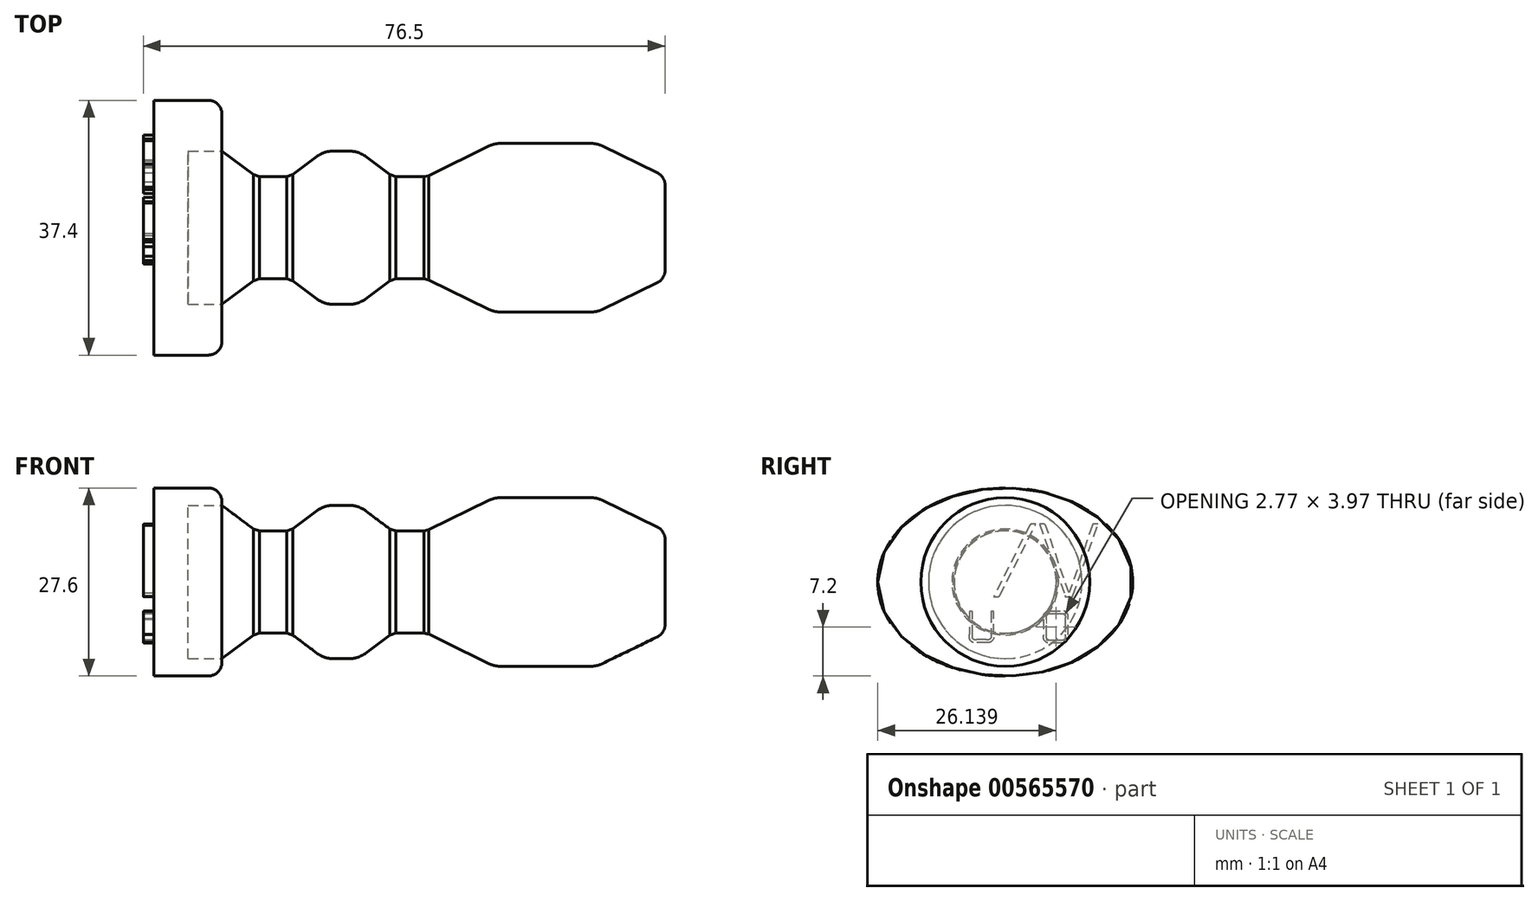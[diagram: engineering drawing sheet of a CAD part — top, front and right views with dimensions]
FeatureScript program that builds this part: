
annotation { "Feature Type Name" : "Feature", "Feature Type Description" : "" }
export const myFeature = defineFeature(function(context is Context, id is Id, definition is map)
    precondition{}
    {
        {
            var Q0;
            Q0=qCreatedBy(makeId("Top.planeOp"),FACE);
            var sketch = newSketch(context, id + "F0", { "sketchPlane" : qUnion([Q0])});
            skLineSegment(sketch, "E0", {"start": v(0, 0) * mm, "end": v(0, -25) * mm});
            skLineSegment(sketch, "E1", {"start": v(0, -25) * mm, "end": v(10, -25) * mm});
            skLineSegment(sketch, "E2", {"start": v(10, -25) * mm, "end": v(10, -11.25) * mm});
            skLineSegment(sketch, "E3", {"start": v(10, -11.25) * mm, "end": v(15, -7.5) * mm});
            skLineSegment(sketch, "E4", {"start": v(15, -7.5) * mm, "end": v(20, -7.5) * mm});
            skLineSegment(sketch, "E5", {"start": v(20, -7.5) * mm, "end": v(25, -11.25) * mm});
            skLineSegment(sketch, "E6", {"start": v(25, -11.25) * mm, "end": v(30, -11.25) * mm});
            skLineSegment(sketch, "E7", {"start": v(30, -11.25) * mm, "end": v(35, -7.5) * mm});
            skLineSegment(sketch, "E8", {"start": v(35, -7.5) * mm, "end": v(40, -7.5) * mm});
            skLineSegment(sketch, "E9", {"start": v(40, -7.5) * mm, "end": v(50, -12.38) * mm});
            skLineSegment(sketch, "E10", {"start": v(50, -12.38) * mm, "end": v(65, -12.38) * mm});
            skLineSegment(sketch, "E11", {"start": v(65, -12.38) * mm, "end": v(75, -7.5) * mm});
            skLineSegment(sketch, "E12", {"start": v(75, -7.5) * mm, "end": v(75, 0) * mm});
            skLineSegment(sketch, "E13", {"start": v(75, 0) * mm, "end": v(0, 0) * mm});
            skLineSegment(sketch, "E14", {"start": v(10, -11.25) * mm, "end": v(10, 0) * mm});
            skLineSegment(sketch, "E15", {"start": v(10, -11.25) * mm, "end": v(0, -11.25) * mm});
            skLineSegment(sketch, "E16", {"start": v(5.06, 0) * mm, "end": v(5.06, -11.25) * mm});
            skLineSegment(sketch, "E17", {"start": v(0, -11.45) * mm, "end": v(10, -11.45) * mm});
            skLineSegment(sketch, "E18", {"start": v(5.06, -11.25) * mm, "end": v(5.06, -11.45) * mm});
            skSolve(sketch);
        }
        {
            var Q0;
            Q0=makeQuery(id+"F0.imprint","IMPRINT",FACE,{"disambiguationData":[TD([[makeQuery(id+"F0.imprint","IMPRINT",EDGE,{"derivedFrom":sQuery(id+"F0.wireOp",EDGE,"E3")}),1.0]])]});
            var Q1;
            {var subQ0=sQuery(id+"F0.wireOp",EDGE,"E14");Q1=makeQuery(id+"F0.imprint","IMPRINT",FACE,{"disambiguationData":[TD([[makeQuery(id+"F0.imprint","IMPRINT",EDGE,{"derivedFrom":subQ0}),1.0]])]});}
            var Q2;
            Q2=sQuery(id+"F0.wireOp",EDGE,"E13");
            revolve(context, id + "F1", {"entities" : qUnion([Q0, Q1]), "axis" : qUnion([Q2]), "revolveType" : RevolveType.FULL});
        }
        {
            var Q0;
            Q0=qCreatedBy(makeId("Right.planeOp"),FACE);
            var sketch = newSketch(context, id + "F2", { "sketchPlane" : qUnion([Q0])});
            skEllipse(sketch, "E19", {"center": v(0, 0) * mm, "majorRadius": 18.7 * mm, "minorRadius": 13.8 * mm, "majorAxis": v(-1, 0)});
            skSolve(sketch);
        }
        {
            var Q0;
            Q0=makeQuery(id+"F2.imprint","IMPRINT",FACE,{"disambiguationData":[TD([[makeQuery(id+"F2.imprint","IMPRINT",EDGE,{"derivedFrom":sQuery(id+"F2.wireOp",EDGE,"E19")}),1.0]])]});
            extrude(context, id + "F3", {"entities" : qUnion([Q0]), "depth" : 10 * mm, "offsetDistance" : 25 * mm});
        }
        {
            var Q0;
            Q0=qCreatedBy(makeId("Right.planeOp"),FACE);
            var sketch = newSketch(context, id + "F4", { "sketchPlane" : qUnion([Q0])});
            skLineSegment(sketch, "E20", {"start": v(-0.44, 1.05) * mm, "end": v(-0.95, 0.16) * mm});
            skLineSegment(sketch, "E21", {"start": v(-0.95, 0.16) * mm, "end": v(-1.46, 1.05) * mm});
            skFitSpline(sketch, "E22", {"points": [v(-1.46, 1.05) * mm, v(-1.46, 1.06) * mm, v(-1.47, 1.06) * mm, v(-1.48, 1.06) * mm]});
            skLineSegment(sketch, "E23", {"start": v(-1.48, 1.06) * mm, "end": v(-1.59, 1.06) * mm});
            skLineSegment(sketch, "E24", {"start": v(-1.59, 1.06) * mm, "end": v(-1.59, -0.27) * mm});
            skLineSegment(sketch, "E25", {"start": v(-1.59, -0.27) * mm, "end": v(-1.52, -0.27) * mm});
            skFitSpline(sketch, "E26", {"points": [v(-1.52, -0.27) * mm, v(-1.5, -0.27) * mm, v(-1.5, -0.26) * mm, v(-1.5, -0.25) * mm]});
            skLineSegment(sketch, "E27", {"start": v(-1.5, -0.25) * mm, "end": v(-1.5, 0.94) * mm});
            skLineSegment(sketch, "E28", {"start": v(-1.5, 0.94) * mm, "end": v(-1.02, 0.1) * mm});
            skFitSpline(sketch, "E29", {"points": [v(-1.02, 0.1) * mm, v(-1.02, 0.08) * mm, v(-1, 0.08) * mm, v(-1, 0.08) * mm]});
            skLineSegment(sketch, "E30", {"start": v(-1, 0.08) * mm, "end": v(-0.91, 0.08) * mm});
            skFitSpline(sketch, "E31", {"points": [v(-0.91, 0.08) * mm, v(-0.9, 0.08) * mm, v(-0.9, 0.08) * mm, v(-0.89, 0.1) * mm]});
            skLineSegment(sketch, "E32", {"start": v(-0.4, 0.94) * mm, "end": v(-0.4, -0.25) * mm});
            skFitSpline(sketch, "E33", {"points": [v(-0.4, -0.25) * mm, v(-0.4, -0.26) * mm, v(-0.4, -0.27) * mm, v(-0.39, -0.27) * mm]});
            skLineSegment(sketch, "E34", {"start": v(-0.39, -0.27) * mm, "end": v(-0.32, -0.27) * mm});
            skLineSegment(sketch, "E35", {"start": v(-0.32, -0.27) * mm, "end": v(-0.32, 1.06) * mm});
            skLineSegment(sketch, "E36", {"start": v(-0.32, 1.06) * mm, "end": v(-0.43, 1.06) * mm});
            skFitSpline(sketch, "E37", {"points": [v(-0.43, 1.06) * mm, v(-0.43, 1.06) * mm, v(-0.44, 1.06) * mm, v(-0.44, 1.05) * mm]});
            skLineSegment(sketch, "E38", {"start": v(0.45, 1.04) * mm, "end": v(-0.21, -0.27) * mm});
            skLineSegment(sketch, "E39", {"start": v(-0.21, -0.27) * mm, "end": v(-0.14, -0.27) * mm});
            skFitSpline(sketch, "E40", {"points": [v(-0.14, -0.27) * mm, v(-0.13, -0.27) * mm, v(-0.11, -0.26) * mm, v(-0.1, -0.25) * mm]});
            skLineSegment(sketch, "E41", {"start": v(-0.1, -0.25) * mm, "end": v(0.56, 1.06) * mm});
            skLineSegment(sketch, "E42", {"start": v(0.56, 1.06) * mm, "end": v(0.48, 1.06) * mm});
            skFitSpline(sketch, "E43", {"points": [v(0.48, 1.06) * mm, v(0.47, 1.06) * mm, v(0.46, 1.05) * mm, v(0.45, 1.04) * mm]});
            skFitSpline(sketch, "E44", {"points": [v(1.1, -0.25) * mm, v(1.1, -0.26) * mm, v(1.1, -0.27) * mm, v(1.12, -0.27) * mm]});
            skLineSegment(sketch, "E45", {"start": v(1.12, -0.27) * mm, "end": v(1.22, -0.27) * mm});
            skFitSpline(sketch, "E46", {"points": [v(1.22, -0.27) * mm, v(1.23, -0.27) * mm, v(1.24, -0.26) * mm, v(1.24, -0.25) * mm]});
            skLineSegment(sketch, "E47", {"start": v(1.24, -0.25) * mm, "end": v(1.7, 1.06) * mm});
            skLineSegment(sketch, "E48", {"start": v(1.7, 1.06) * mm, "end": v(1.63, 1.06) * mm});
            skFitSpline(sketch, "E49", {"points": [v(1.63, 1.06) * mm, v(1.62, 1.06) * mm, v(1.6, 1.05) * mm, v(1.6, 1.04) * mm]});
            skLineSegment(sketch, "E50", {"start": v(1.6, 1.04) * mm, "end": v(1.17, -0.2) * mm});
            skLineSegment(sketch, "E51", {"start": v(1.17, -0.2) * mm, "end": v(0.74, 1.04) * mm});
            skFitSpline(sketch, "E52", {"points": [v(0.74, 1.04) * mm, v(0.73, 1.05) * mm, v(0.72, 1.06) * mm, v(0.7, 1.06) * mm]});
            skLineSegment(sketch, "E53", {"start": v(0.7, 1.06) * mm, "end": v(0.63, 1.06) * mm});
            skLineSegment(sketch, "E54", {"start": v(0.63, 1.06) * mm, "end": v(1.1, -0.25) * mm});
            skLineSegment(sketch, "E55", {"start": v(-1.2, -0.9) * mm, "end": v(-1.2, -0.98) * mm});
            skFitSpline(sketch, "E56", {"points": [v(-1.2, -0.98) * mm, v(-1.2, -1.03) * mm, v(-1.25, -1.06) * mm, v(-1.3, -1.06) * mm]});
            skLineSegment(sketch, "E57", {"start": v(-1.3, -1.06) * mm, "end": v(-1.58, -1.06) * mm});
            skFitSpline(sketch, "E58", {"points": [v(-1.58, -1.06) * mm, v(-1.59, -1.06) * mm, v(-1.6, -1.06) * mm, v(-1.6, -1.07) * mm]});
            skLineSegment(sketch, "E59", {"start": v(-1.6, -1.07) * mm, "end": v(-1.6, -1.1) * mm});
            skLineSegment(sketch, "E60", {"start": v(-1.6, -1.1) * mm, "end": v(-1.3, -1.1) * mm});
            skFitSpline(sketch, "E61", {"points": [v(-1.3, -1.1) * mm, v(-1.22, -1.1) * mm, v(-1.15, -1.06) * mm, v(-1.15, -0.98) * mm]});
            skLineSegment(sketch, "E62", {"start": v(-1.15, -0.98) * mm, "end": v(-1.15, -0.9) * mm});
            skFitSpline(sketch, "E63", {"points": [v(-1.15, -0.9) * mm, v(-1.15, -0.88) * mm, v(-1.17, -0.86) * mm, v(-1.18, -0.85) * mm]});
            skLineSegment(sketch, "E64", {"start": v(-1.18, -0.85) * mm, "end": v(-1.53, -0.73) * mm});
            skFitSpline(sketch, "E65", {"points": [v(-1.53, -0.73) * mm, v(-1.54, -0.73) * mm, v(-1.54, -0.72) * mm, v(-1.54, -0.71) * mm]});
            skLineSegment(sketch, "E66", {"start": v(-1.54, -0.71) * mm, "end": v(-1.54, -0.67) * mm});
            skFitSpline(sketch, "E67", {"points": [v(-1.54, -0.67) * mm, v(-1.54, -0.62) * mm, v(-1.5, -0.6) * mm, v(-1.45, -0.6) * mm]});
            skLineSegment(sketch, "E68", {"start": v(-1.45, -0.6) * mm, "end": v(-1.2, -0.6) * mm});
            skFitSpline(sketch, "E69", {"points": [v(-1.2, -0.6) * mm, v(-1.2, -0.6) * mm, v(-1.2, -0.58) * mm, v(-1.2, -0.58) * mm]});
            skLineSegment(sketch, "E70", {"start": v(-1.2, -0.58) * mm, "end": v(-1.2, -0.54) * mm});
            skLineSegment(sketch, "E71", {"start": v(-1.2, -0.54) * mm, "end": v(-1.45, -0.54) * mm});
            skFitSpline(sketch, "E72", {"points": [v(-1.45, -0.54) * mm, v(-1.53, -0.54) * mm, v(-1.6, -0.6) * mm, v(-1.6, -0.67) * mm]});
            skLineSegment(sketch, "E73", {"start": v(-1.6, -0.67) * mm, "end": v(-1.6, -0.73) * mm});
            skFitSpline(sketch, "E74", {"points": [v(-1.6, -0.73) * mm, v(-1.6, -0.74) * mm, v(-1.58, -0.76) * mm, v(-1.56, -0.77) * mm]});
            skLineSegment(sketch, "E75", {"start": v(-1.56, -0.77) * mm, "end": v(-1.21, -0.9) * mm});
            skFitSpline(sketch, "E76", {"points": [v(-1.21, -0.9) * mm, v(-1.2, -0.9) * mm, v(-1.2, -0.9) * mm, v(-1.2, -0.9) * mm]});
            skLineSegment(sketch, "E77", {"start": v(-0.78, -1.06) * mm, "end": v(-0.88, -1.06) * mm});
            skFitSpline(sketch, "E78", {"points": [v(-0.88, -1.06) * mm, v(-0.93, -1.06) * mm, v(-0.97, -1.02) * mm, v(-0.97, -0.97) * mm]});
            skLineSegment(sketch, "E79", {"start": v(-0.97, -0.97) * mm, "end": v(-0.97, -0.6) * mm});
            skLineSegment(sketch, "E80", {"start": v(-0.97, -0.6) * mm, "end": v(-0.81, -0.6) * mm});
            skFitSpline(sketch, "E81", {"points": [v(-0.81, -0.6) * mm, v(-0.8, -0.6) * mm, v(-0.8, -0.59) * mm, v(-0.8, -0.58) * mm]});
            skLineSegment(sketch, "E82", {"start": v(-0.8, -0.58) * mm, "end": v(-0.8, -0.55) * mm});
            skLineSegment(sketch, "E83", {"start": v(-0.8, -0.55) * mm, "end": v(-0.94, -0.55) * mm});
            skFitSpline(sketch, "E84", {"points": [v(-0.94, -0.55) * mm, v(-0.95, -0.55) * mm, v(-0.97, -0.55) * mm, v(-0.97, -0.57) * mm]});
            skLineSegment(sketch, "E85", {"start": v(-0.97, -0.57) * mm, "end": v(-0.97, -0.27) * mm});
            skFitSpline(sketch, "E86", {"points": [v(-0.97, -0.27) * mm, v(-0.97, -0.27) * mm, v(-0.97, -0.26) * mm, v(-0.98, -0.26) * mm]});
            skLineSegment(sketch, "E87", {"start": v(-0.98, -0.26) * mm, "end": v(-1.02, -0.26) * mm});
            skLineSegment(sketch, "E88", {"start": v(-1.02, -0.26) * mm, "end": v(-1.02, -0.96) * mm});
            skFitSpline(sketch, "E89", {"points": [v(-1.02, -0.96) * mm, v(-1.02, -1.04) * mm, v(-0.96, -1.1) * mm, v(-0.88, -1.1) * mm]});
            skLineSegment(sketch, "E90", {"start": v(-0.88, -1.1) * mm, "end": v(-0.77, -1.1) * mm});
            skLineSegment(sketch, "E91", {"start": v(-0.77, -1.1) * mm, "end": v(-0.77, -1.07) * mm});
            skFitSpline(sketch, "E92", {"points": [v(-0.77, -1.07) * mm, v(-0.77, -1.06) * mm, v(-0.77, -1.06) * mm, v(-0.78, -1.06) * mm]});
            skFitSpline(sketch, "E93", {"points": [v(-0.66, -0.96) * mm, v(-0.66, -1.04) * mm, v(-0.6, -1.1) * mm, v(-0.52, -1.1) * mm]});
            skLineSegment(sketch, "E94", {"start": v(-0.52, -1.1) * mm, "end": v(-0.35, -1.1) * mm});
            skFitSpline(sketch, "E95", {"points": [v(-0.35, -1.1) * mm, v(-0.28, -1.1) * mm, v(-0.21, -1.04) * mm, v(-0.21, -0.96) * mm]});
            skLineSegment(sketch, "E96", {"start": v(-0.21, -0.96) * mm, "end": v(-0.21, -0.54) * mm});
            skLineSegment(sketch, "E97", {"start": v(-0.21, -0.54) * mm, "end": v(-0.25, -0.54) * mm});
            skFitSpline(sketch, "E98", {"points": [v(-0.25, -0.54) * mm, v(-0.26, -0.54) * mm, v(-0.26, -0.55) * mm, v(-0.26, -0.56) * mm]});
            skLineSegment(sketch, "E99", {"start": v(-0.26, -0.56) * mm, "end": v(-0.26, -0.97) * mm});
            skFitSpline(sketch, "E100", {"points": [v(-0.26, -0.97) * mm, v(-0.26, -1.02) * mm, v(-0.3, -1.06) * mm, v(-0.35, -1.06) * mm]});
            skLineSegment(sketch, "E101", {"start": v(-0.35, -1.06) * mm, "end": v(-0.52, -1.06) * mm});
            skFitSpline(sketch, "E102", {"points": [v(-0.52, -1.06) * mm, v(-0.57, -1.06) * mm, v(-0.6, -1.02) * mm, v(-0.6, -0.97) * mm]});
            skLineSegment(sketch, "E103", {"start": v(-0.6, -0.97) * mm, "end": v(-0.6, -0.56) * mm});
            skFitSpline(sketch, "E104", {"points": [v(-0.6, -0.56) * mm, v(-0.6, -0.55) * mm, v(-0.61, -0.54) * mm, v(-0.62, -0.54) * mm]});
            skLineSegment(sketch, "E105", {"start": v(-0.62, -0.54) * mm, "end": v(-0.66, -0.54) * mm});
            skLineSegment(sketch, "E106", {"start": v(-0.66, -0.54) * mm, "end": v(-0.66, -0.96) * mm});
            skFitSpline(sketch, "E107", {"points": [v(0.32, -0.26) * mm, v(0.31, -0.26) * mm, v(0.3, -0.27) * mm, v(0.3, -0.28) * mm]});
            skLineSegment(sketch, "E108", {"start": v(0.3, -0.28) * mm, "end": v(0.3, -0.57) * mm});
            skFitSpline(sketch, "E109", {"points": [v(0.3, -0.57) * mm, v(0.3, -0.55) * mm, v(0.3, -0.54) * mm, v(0.28, -0.54) * mm]});
            skLineSegment(sketch, "E110", {"start": v(0.28, -0.54) * mm, "end": v(0.06, -0.54) * mm});
            skFitSpline(sketch, "E111", {"points": [v(0.06, -0.54) * mm, v(-0.02, -0.54) * mm, v(-0.08, -0.6) * mm, v(-0.08, -0.68) * mm]});
            skLineSegment(sketch, "E112", {"start": v(-0.08, -0.68) * mm, "end": v(-0.08, -0.96) * mm});
            skFitSpline(sketch, "E113", {"points": [v(-0.08, -0.96) * mm, v(-0.08, -1.04) * mm, v(-0.02, -1.1) * mm, v(0.06, -1.1) * mm]});
            skLineSegment(sketch, "E114", {"start": v(0.06, -1.1) * mm, "end": v(0.35, -1.1) * mm});
            skFitSpline(sketch, "E115", {"points": [v(0.35, -1.1) * mm, v(0.35, -1.1) * mm, v(0.36, -1.1) * mm, v(0.36, -1.1) * mm]});
            skLineSegment(sketch, "E116", {"start": v(0.36, -1.1) * mm, "end": v(0.36, -0.26) * mm});
            skLineSegment(sketch, "E117", {"start": v(0.36, -0.26) * mm, "end": v(0.32, -0.26) * mm});
            skFitSpline(sketch, "E118", {"points": [v(0.06, -1.06) * mm, v(0, -1.06) * mm, v(-0.03, -1.02) * mm, v(-0.03, -0.97) * mm]});
            skLineSegment(sketch, "E119", {"start": v(-0.03, -0.97) * mm, "end": v(-0.03, -0.68) * mm});
            skFitSpline(sketch, "E120", {"points": [v(-0.03, -0.68) * mm, v(-0.03, -0.63) * mm, v(0, -0.6) * mm, v(0.06, -0.6) * mm]});
            skLineSegment(sketch, "E121", {"start": v(0.06, -0.6) * mm, "end": v(0.29, -0.6) * mm});
            skFitSpline(sketch, "E122", {"points": [v(0.29, -0.6) * mm, v(0.3, -0.6) * mm, v(0.3, -0.6) * mm, v(0.3, -0.61) * mm]});
            skLineSegment(sketch, "E123", {"start": v(0.3, -0.61) * mm, "end": v(0.3, -1.06) * mm});
            skLineSegment(sketch, "E124", {"start": v(0.3, -1.06) * mm, "end": v(0.06, -1.06) * mm});
            skFitSpline(sketch, "E125", {"points": [v(0.5, -1.1) * mm, v(0.5, -1.1) * mm, v(0.5, -1.1) * mm, v(0.5, -1.1) * mm]});
            skLineSegment(sketch, "E126", {"start": v(0.5, -1.1) * mm, "end": v(0.55, -1.1) * mm});
            skLineSegment(sketch, "E127", {"start": v(0.55, -1.1) * mm, "end": v(0.55, -0.56) * mm});
            skFitSpline(sketch, "E128", {"points": [v(0.55, -0.56) * mm, v(0.55, -0.55) * mm, v(0.54, -0.54) * mm, v(0.53, -0.54) * mm]});
            skLineSegment(sketch, "E129", {"start": v(0.53, -0.54) * mm, "end": v(0.5, -0.54) * mm});
            skLineSegment(sketch, "E130", {"start": v(0.5, -0.54) * mm, "end": v(0.5, -1.1) * mm});
            skFitSpline(sketch, "E131", {"points": [v(0.5, -0.35) * mm, v(0.5, -0.36) * mm, v(0.5, -0.36) * mm, v(0.5, -0.36) * mm]});
            skLineSegment(sketch, "E132", {"start": v(0.5, -0.36) * mm, "end": v(0.55, -0.36) * mm});
            skLineSegment(sketch, "E133", {"start": v(0.55, -0.36) * mm, "end": v(0.55, -0.3) * mm});
            skFitSpline(sketch, "E134", {"points": [v(0.55, -0.3) * mm, v(0.55, -0.3) * mm, v(0.54, -0.3) * mm, v(0.54, -0.3) * mm]});
            skLineSegment(sketch, "E135", {"start": v(0.54, -0.3) * mm, "end": v(0.5, -0.3) * mm});
            skLineSegment(sketch, "E136", {"start": v(0.5, -0.3) * mm, "end": v(0.5, -0.35) * mm});
            skFitSpline(sketch, "E137", {"points": [v(1.01, -1.11) * mm, v(1.1, -1.11) * mm, v(1.15, -1.05) * mm, v(1.15, -0.97) * mm]});
            skLineSegment(sketch, "E138", {"start": v(1.15, -0.97) * mm, "end": v(1.15, -0.68) * mm});
            skFitSpline(sketch, "E139", {"points": [v(1.15, -0.68) * mm, v(1.15, -0.6) * mm, v(1.1, -0.54) * mm, v(1.01, -0.54) * mm]});
            skLineSegment(sketch, "E140", {"start": v(1.01, -0.54) * mm, "end": v(0.84, -0.54) * mm});
            skFitSpline(sketch, "E141", {"points": [v(0.84, -0.54) * mm, v(0.77, -0.54) * mm, v(0.7, -0.6) * mm, v(0.7, -0.68) * mm]});
            skLineSegment(sketch, "E142", {"start": v(0.7, -0.68) * mm, "end": v(0.7, -0.97) * mm});
            skFitSpline(sketch, "E143", {"points": [v(0.7, -0.97) * mm, v(0.7, -1.05) * mm, v(0.77, -1.11) * mm, v(0.84, -1.11) * mm]});
            skLineSegment(sketch, "E144", {"start": v(0.84, -1.11) * mm, "end": v(1.01, -1.11) * mm});
            skFitSpline(sketch, "E145", {"points": [v(1.01, -0.58) * mm, v(1.06, -0.58) * mm, v(1.1, -0.62) * mm, v(1.1, -0.67) * mm]});
            skLineSegment(sketch, "E146", {"start": v(1.1, -0.67) * mm, "end": v(1.1, -0.98) * mm});
            skFitSpline(sketch, "E147", {"points": [v(1.1, -0.98) * mm, v(1.1, -1.03) * mm, v(1.06, -1.07) * mm, v(1.01, -1.07) * mm]});
            skLineSegment(sketch, "E148", {"start": v(1.01, -1.07) * mm, "end": v(0.84, -1.07) * mm});
            skFitSpline(sketch, "E149", {"points": [v(0.84, -1.07) * mm, v(0.8, -1.07) * mm, v(0.76, -1.03) * mm, v(0.76, -0.98) * mm]});
            skLineSegment(sketch, "E150", {"start": v(0.76, -0.98) * mm, "end": v(0.76, -0.67) * mm});
            skFitSpline(sketch, "E151", {"points": [v(0.76, -0.67) * mm, v(0.76, -0.62) * mm, v(0.8, -0.58) * mm, v(0.84, -0.58) * mm]});
            skLineSegment(sketch, "E152", {"start": v(0.84, -0.58) * mm, "end": v(1.01, -0.58) * mm});
            skLineSegment(sketch, "E153", {"start": v(1.67, -0.9) * mm, "end": v(1.67, -0.98) * mm});
            skFitSpline(sketch, "E154", {"points": [v(1.67, -0.98) * mm, v(1.67, -1.03) * mm, v(1.63, -1.06) * mm, v(1.58, -1.06) * mm]});
            skLineSegment(sketch, "E155", {"start": v(1.58, -1.06) * mm, "end": v(1.29, -1.06) * mm});
            skFitSpline(sketch, "E156", {"points": [v(1.29, -1.06) * mm, v(1.28, -1.06) * mm, v(1.28, -1.06) * mm, v(1.28, -1.07) * mm]});
            skLineSegment(sketch, "E157", {"start": v(1.28, -1.07) * mm, "end": v(1.28, -1.1) * mm});
            skLineSegment(sketch, "E158", {"start": v(1.28, -1.1) * mm, "end": v(1.58, -1.1) * mm});
            skFitSpline(sketch, "E159", {"points": [v(1.58, -1.1) * mm, v(1.65, -1.1) * mm, v(1.72, -1.06) * mm, v(1.72, -0.98) * mm]});
            skLineSegment(sketch, "E160", {"start": v(1.72, -0.98) * mm, "end": v(1.72, -0.9) * mm});
            skFitSpline(sketch, "E161", {"points": [v(1.72, -0.9) * mm, v(1.72, -0.88) * mm, v(1.7, -0.86) * mm, v(1.69, -0.85) * mm]});
            skLineSegment(sketch, "E162", {"start": v(1.69, -0.85) * mm, "end": v(1.34, -0.73) * mm});
            skFitSpline(sketch, "E163", {"points": [v(1.34, -0.73) * mm, v(1.33, -0.73) * mm, v(1.33, -0.72) * mm, v(1.33, -0.71) * mm]});
            skLineSegment(sketch, "E164", {"start": v(1.33, -0.71) * mm, "end": v(1.33, -0.67) * mm});
            skFitSpline(sketch, "E165", {"points": [v(1.33, -0.67) * mm, v(1.33, -0.62) * mm, v(1.37, -0.6) * mm, v(1.42, -0.6) * mm]});
            skLineSegment(sketch, "E166", {"start": v(1.42, -0.6) * mm, "end": v(1.66, -0.6) * mm});
            skFitSpline(sketch, "E167", {"points": [v(1.66, -0.6) * mm, v(1.67, -0.6) * mm, v(1.67, -0.58) * mm, v(1.67, -0.58) * mm]});
            skLineSegment(sketch, "E168", {"start": v(1.67, -0.58) * mm, "end": v(1.67, -0.54) * mm});
            skLineSegment(sketch, "E169", {"start": v(1.67, -0.54) * mm, "end": v(1.42, -0.54) * mm});
            skFitSpline(sketch, "E170", {"points": [v(1.42, -0.54) * mm, v(1.34, -0.54) * mm, v(1.28, -0.6) * mm, v(1.28, -0.67) * mm]});
            skLineSegment(sketch, "E171", {"start": v(1.28, -0.67) * mm, "end": v(1.28, -0.73) * mm});
            skFitSpline(sketch, "E172", {"points": [v(1.28, -0.73) * mm, v(1.28, -0.74) * mm, v(1.3, -0.76) * mm, v(1.3, -0.77) * mm]});
            skLineSegment(sketch, "E173", {"start": v(1.3, -0.77) * mm, "end": v(1.66, -0.9) * mm});
            skFitSpline(sketch, "E174", {"points": [v(1.66, -0.9) * mm, v(1.66, -0.9) * mm, v(1.67, -0.9) * mm, v(1.67, -0.9) * mm]});
            skLineSegment(sketch, "E175", {"start": v(-0.4, 0.94) * mm, "end": v(-0.89, 0.1) * mm});
            skSolve(sketch);
        }
        {
            var Q0;
            Q0=makeQuery(id+"F4.imprint","IMPRINT",FACE,{"disambiguationData":[TD([[makeQuery(id+"F4.imprint","IMPRINT",EDGE,{"derivedFrom":sQuery(id+"F4.wireOp",EDGE,"E38")}),1.0]])]});
            var Q1;
            Q1=makeQuery(id+"F4.imprint","IMPRINT",FACE,{"disambiguationData":[TD([[makeQuery(id+"F4.imprint","IMPRINT",EDGE,{"derivedFrom":sQuery(id+"F4.wireOp",EDGE,"E44")}),1.0]])]});
            var Q2;
            Q2=makeQuery(id+"F4.imprint","IMPRINT",FACE,{"disambiguationData":[TD([[makeQuery(id+"F4.imprint","IMPRINT",EDGE,{"derivedFrom":sQuery(id+"F4.wireOp",EDGE,"E137")}),1.0]])]});
            var Q3;
            Q3=makeQuery(id+"F4.imprint","IMPRINT",FACE,{"disambiguationData":[TD([[makeQuery(id+"F4.imprint","IMPRINT",EDGE,{"derivedFrom":sQuery(id+"F4.wireOp",EDGE,"E153")}),1.0]])]});
            var Q4;
            Q4=makeQuery(id+"F4.imprint","IMPRINT",FACE,{"disambiguationData":[TD([[makeQuery(id+"F4.imprint","IMPRINT",EDGE,{"derivedFrom":sQuery(id+"F4.wireOp",EDGE,"E125")}),1.0]])]});
            var Q5;
            Q5=makeQuery(id+"F4.imprint","IMPRINT",FACE,{"disambiguationData":[TD([[makeQuery(id+"F4.imprint","IMPRINT",EDGE,{"derivedFrom":sQuery(id+"F4.wireOp",EDGE,"E131")}),1.0]])]});
            var Q6;
            Q6=makeQuery(id+"F4.imprint","IMPRINT",FACE,{"disambiguationData":[TD([[makeQuery(id+"F4.imprint","IMPRINT",EDGE,{"derivedFrom":sQuery(id+"F4.wireOp",EDGE,"E107")}),1.0]])]});
            var Q7;
            Q7=makeQuery(id+"F4.imprint","IMPRINT",FACE,{"disambiguationData":[TD([[makeQuery(id+"F4.imprint","IMPRINT",EDGE,{"derivedFrom":sQuery(id+"F4.wireOp",EDGE,"E93")}),1.0]])]});
            var Q8;
            Q8=makeQuery(id+"F4.imprint","IMPRINT",FACE,{"disambiguationData":[TD([[makeQuery(id+"F4.imprint","IMPRINT",EDGE,{"derivedFrom":sQuery(id+"F4.wireOp",EDGE,"E77")}),1.0]])]});
            var Q9;
            Q9=makeQuery(id+"F4.imprint","IMPRINT",FACE,{"disambiguationData":[TD([[makeQuery(id+"F4.imprint","IMPRINT",EDGE,{"derivedFrom":sQuery(id+"F4.wireOp",EDGE,"E55")}),1.0]])]});
            var Q10;
            Q10=makeQuery(id+"F4.imprint","IMPRINT",FACE,{"disambiguationData":[TD([[makeQuery(id+"F4.imprint","IMPRINT",EDGE,{"derivedFrom":sQuery(id+"F4.wireOp",EDGE,"E20")}),1.0]])]});
            extrude(context, id + "F5", {"entities" : qUnion([Q0, Q1, Q2, Q3, Q4, Q5, Q6, Q7, Q8, Q9, Q10]), "depth" : (-1.5 / 8) * mm, "offsetDistance" : 25 * mm});
        }
        {
            var Q0;
            Q0=makeQuery(id+"F5.opExtrude","SWEPT_BODY",BODY,{"disambiguationData":[OSD([sQuery(id+"F4.wireOp",EDGE,"E137"),sQuery(id+"F4.wireOp",EDGE,"E138"),sQuery(id+"F4.wireOp",EDGE,"E139"),sQuery(id+"F4.wireOp",EDGE,"E140"),sQuery(id+"F4.wireOp",EDGE,"E141"),sQuery(id+"F4.wireOp",EDGE,"E142"),sQuery(id+"F4.wireOp",EDGE,"E143"),sQuery(id+"F4.wireOp",EDGE,"E144"),sQuery(id+"F4.wireOp",EDGE,"E145"),sQuery(id+"F4.wireOp",EDGE,"E146"),sQuery(id+"F4.wireOp",EDGE,"E147"),sQuery(id+"F4.wireOp",EDGE,"E148"),sQuery(id+"F4.wireOp",EDGE,"E149"),sQuery(id+"F4.wireOp",EDGE,"E150"),sQuery(id+"F4.wireOp",EDGE,"E151"),sQuery(id+"F4.wireOp",EDGE,"E152")])]});
            var Q1;
            Q1=makeQuery(id+"F5.opExtrude","SWEPT_BODY",BODY,{"disambiguationData":[OSD([sQuery(id+"F4.wireOp",EDGE,"E44"),sQuery(id+"F4.wireOp",EDGE,"E45"),sQuery(id+"F4.wireOp",EDGE,"E46"),sQuery(id+"F4.wireOp",EDGE,"E47"),sQuery(id+"F4.wireOp",EDGE,"E48"),sQuery(id+"F4.wireOp",EDGE,"E49"),sQuery(id+"F4.wireOp",EDGE,"E50"),sQuery(id+"F4.wireOp",EDGE,"E51"),sQuery(id+"F4.wireOp",EDGE,"E52"),sQuery(id+"F4.wireOp",EDGE,"E53"),sQuery(id+"F4.wireOp",EDGE,"E54")])]});
            var Q2;
            Q2=makeQuery(id+"F5.opExtrude","SWEPT_BODY",BODY,{"disambiguationData":[OSD([sQuery(id+"F4.wireOp",EDGE,"E153"),sQuery(id+"F4.wireOp",EDGE,"E154"),sQuery(id+"F4.wireOp",EDGE,"E155"),sQuery(id+"F4.wireOp",EDGE,"E156"),sQuery(id+"F4.wireOp",EDGE,"E157"),sQuery(id+"F4.wireOp",EDGE,"E158"),sQuery(id+"F4.wireOp",EDGE,"E159"),sQuery(id+"F4.wireOp",EDGE,"E160"),sQuery(id+"F4.wireOp",EDGE,"E161"),sQuery(id+"F4.wireOp",EDGE,"E162"),sQuery(id+"F4.wireOp",EDGE,"E163"),sQuery(id+"F4.wireOp",EDGE,"E164"),sQuery(id+"F4.wireOp",EDGE,"E165"),sQuery(id+"F4.wireOp",EDGE,"E166"),sQuery(id+"F4.wireOp",EDGE,"E167"),sQuery(id+"F4.wireOp",EDGE,"E168"),sQuery(id+"F4.wireOp",EDGE,"E169"),sQuery(id+"F4.wireOp",EDGE,"E170"),sQuery(id+"F4.wireOp",EDGE,"E171"),sQuery(id+"F4.wireOp",EDGE,"E172"),sQuery(id+"F4.wireOp",EDGE,"E173"),sQuery(id+"F4.wireOp",EDGE,"E174")])]});
            var Q3;
            Q3=makeQuery(id+"F5.opExtrude","SWEPT_BODY",BODY,{"disambiguationData":[OSD([sQuery(id+"F4.wireOp",EDGE,"E125"),sQuery(id+"F4.wireOp",EDGE,"E126"),sQuery(id+"F4.wireOp",EDGE,"E127"),sQuery(id+"F4.wireOp",EDGE,"E128"),sQuery(id+"F4.wireOp",EDGE,"E129"),sQuery(id+"F4.wireOp",EDGE,"E130")])]});
            var Q4;
            Q4=makeQuery(id+"F5.opExtrude","SWEPT_BODY",BODY,{"disambiguationData":[OSD([sQuery(id+"F4.wireOp",EDGE,"E131"),sQuery(id+"F4.wireOp",EDGE,"E132"),sQuery(id+"F4.wireOp",EDGE,"E133"),sQuery(id+"F4.wireOp",EDGE,"E134"),sQuery(id+"F4.wireOp",EDGE,"E135"),sQuery(id+"F4.wireOp",EDGE,"E136")])]});
            var Q5;
            Q5=makeQuery(id+"F5.opExtrude","SWEPT_BODY",BODY,{"disambiguationData":[OSD([sQuery(id+"F4.wireOp",EDGE,"E38"),sQuery(id+"F4.wireOp",EDGE,"E39"),sQuery(id+"F4.wireOp",EDGE,"E40"),sQuery(id+"F4.wireOp",EDGE,"E41"),sQuery(id+"F4.wireOp",EDGE,"E42"),sQuery(id+"F4.wireOp",EDGE,"E43")])]});
            var Q6;
            Q6=makeQuery(id+"F5.opExtrude","SWEPT_BODY",BODY,{"disambiguationData":[OSD([sQuery(id+"F4.wireOp",EDGE,"E20"),sQuery(id+"F4.wireOp",EDGE,"E21"),sQuery(id+"F4.wireOp",EDGE,"E22"),sQuery(id+"F4.wireOp",EDGE,"E23"),sQuery(id+"F4.wireOp",EDGE,"E24"),sQuery(id+"F4.wireOp",EDGE,"E25"),sQuery(id+"F4.wireOp",EDGE,"E26"),sQuery(id+"F4.wireOp",EDGE,"E27"),sQuery(id+"F4.wireOp",EDGE,"E28"),sQuery(id+"F4.wireOp",EDGE,"E29"),sQuery(id+"F4.wireOp",EDGE,"E30"),sQuery(id+"F4.wireOp",EDGE,"E31"),sQuery(id+"F4.wireOp",EDGE,"E32"),sQuery(id+"F4.wireOp",EDGE,"E33"),sQuery(id+"F4.wireOp",EDGE,"E34"),sQuery(id+"F4.wireOp",EDGE,"E35"),sQuery(id+"F4.wireOp",EDGE,"E36"),sQuery(id+"F4.wireOp",EDGE,"E37"),sQuery(id+"F4.wireOp",EDGE,"E175")])]});
            var Q7;
            Q7=makeQuery(id+"F5.opExtrude","SWEPT_BODY",BODY,{"disambiguationData":[OSD([sQuery(id+"F4.wireOp",EDGE,"E93"),sQuery(id+"F4.wireOp",EDGE,"E94"),sQuery(id+"F4.wireOp",EDGE,"E95"),sQuery(id+"F4.wireOp",EDGE,"E96"),sQuery(id+"F4.wireOp",EDGE,"E97"),sQuery(id+"F4.wireOp",EDGE,"E98"),sQuery(id+"F4.wireOp",EDGE,"E99"),sQuery(id+"F4.wireOp",EDGE,"E100"),sQuery(id+"F4.wireOp",EDGE,"E101"),sQuery(id+"F4.wireOp",EDGE,"E102"),sQuery(id+"F4.wireOp",EDGE,"E103"),sQuery(id+"F4.wireOp",EDGE,"E104"),sQuery(id+"F4.wireOp",EDGE,"E105"),sQuery(id+"F4.wireOp",EDGE,"E106")])]});
            var Q8;
            Q8=makeQuery(id+"F5.opExtrude","SWEPT_BODY",BODY,{"disambiguationData":[OSD([sQuery(id+"F4.wireOp",EDGE,"E77"),sQuery(id+"F4.wireOp",EDGE,"E78"),sQuery(id+"F4.wireOp",EDGE,"E79"),sQuery(id+"F4.wireOp",EDGE,"E80"),sQuery(id+"F4.wireOp",EDGE,"E81"),sQuery(id+"F4.wireOp",EDGE,"E82"),sQuery(id+"F4.wireOp",EDGE,"E83"),sQuery(id+"F4.wireOp",EDGE,"E84"),sQuery(id+"F4.wireOp",EDGE,"E85"),sQuery(id+"F4.wireOp",EDGE,"E86"),sQuery(id+"F4.wireOp",EDGE,"E87"),sQuery(id+"F4.wireOp",EDGE,"E88"),sQuery(id+"F4.wireOp",EDGE,"E89"),sQuery(id+"F4.wireOp",EDGE,"E90"),sQuery(id+"F4.wireOp",EDGE,"E91"),sQuery(id+"F4.wireOp",EDGE,"E92")])]});
            var Q9;
            Q9=makeQuery(id+"F5.opExtrude","SWEPT_BODY",BODY,{"disambiguationData":[OSD([sQuery(id+"F4.wireOp",EDGE,"E55"),sQuery(id+"F4.wireOp",EDGE,"E56"),sQuery(id+"F4.wireOp",EDGE,"E57"),sQuery(id+"F4.wireOp",EDGE,"E58"),sQuery(id+"F4.wireOp",EDGE,"E59"),sQuery(id+"F4.wireOp",EDGE,"E60"),sQuery(id+"F4.wireOp",EDGE,"E61"),sQuery(id+"F4.wireOp",EDGE,"E62"),sQuery(id+"F4.wireOp",EDGE,"E63"),sQuery(id+"F4.wireOp",EDGE,"E64"),sQuery(id+"F4.wireOp",EDGE,"E65"),sQuery(id+"F4.wireOp",EDGE,"E66"),sQuery(id+"F4.wireOp",EDGE,"E67"),sQuery(id+"F4.wireOp",EDGE,"E68"),sQuery(id+"F4.wireOp",EDGE,"E69"),sQuery(id+"F4.wireOp",EDGE,"E70"),sQuery(id+"F4.wireOp",EDGE,"E71"),sQuery(id+"F4.wireOp",EDGE,"E72"),sQuery(id+"F4.wireOp",EDGE,"E73"),sQuery(id+"F4.wireOp",EDGE,"E74"),sQuery(id+"F4.wireOp",EDGE,"E75"),sQuery(id+"F4.wireOp",EDGE,"E76")])]});
            var Q10;
            Q10=makeQuery(id+"F5.opExtrude","SWEPT_BODY",BODY,{"disambiguationData":[OSD([sQuery(id+"F4.wireOp",EDGE,"E107"),sQuery(id+"F4.wireOp",EDGE,"E108"),sQuery(id+"F4.wireOp",EDGE,"E109"),sQuery(id+"F4.wireOp",EDGE,"E110"),sQuery(id+"F4.wireOp",EDGE,"E111"),sQuery(id+"F4.wireOp",EDGE,"E112"),sQuery(id+"F4.wireOp",EDGE,"E113"),sQuery(id+"F4.wireOp",EDGE,"E114"),sQuery(id+"F4.wireOp",EDGE,"E115"),sQuery(id+"F4.wireOp",EDGE,"E116"),sQuery(id+"F4.wireOp",EDGE,"E117"),sQuery(id+"F4.wireOp",EDGE,"E118"),sQuery(id+"F4.wireOp",EDGE,"E119"),sQuery(id+"F4.wireOp",EDGE,"E120"),sQuery(id+"F4.wireOp",EDGE,"E121"),sQuery(id+"F4.wireOp",EDGE,"E122"),sQuery(id+"F4.wireOp",EDGE,"E123"),sQuery(id+"F4.wireOp",EDGE,"E124")])]});
            var Q11;
            Q11=sQuery(id+"F0.wireOp",VERTEX,"E13.end");
            transform(context, id + "F6", {"entities" : qUnion([Q0, Q1, Q2, Q3, Q4, Q5, Q6, Q7, Q8, Q9, Q10]), "transformType" : TransformType.SCALE_UNIFORMLY, "scale" : 8, "scalePoint" : qUnion([Q11]), "makeCopy" : false});
        }
        {
            var Q0;
            Q0=makeQuery(id+"F1.opRevolve","SWEPT_EDGE",EDGE,{"disambiguationData":[OSD([sQuery(id+"F0.wireOp",EDGE,"E10"),sQuery(id+"F0.wireOp",EDGE,"E11")])]});
            var Q1;
            Q1=makeQuery(id+"F1.opRevolve","SWEPT_EDGE",EDGE,{"disambiguationData":[OSD([sQuery(id+"F0.wireOp",EDGE,"E9"),sQuery(id+"F0.wireOp",EDGE,"E10")])]});
            var Q2;
            Q2=makeQuery(id+"F1.opRevolve","SWEPT_EDGE",EDGE,{"disambiguationData":[OSD([sQuery(id+"F0.wireOp",EDGE,"E6"),sQuery(id+"F0.wireOp",EDGE,"E7")])]});
            var Q3;
            Q3=makeQuery(id+"F1.opRevolve","SWEPT_EDGE",EDGE,{"disambiguationData":[OSD([sQuery(id+"F0.wireOp",EDGE,"E5"),sQuery(id+"F0.wireOp",EDGE,"E6")])]});
            fillet(context, id + "F7", {"entities" : qUnion([Q0, Q1, Q2, Q3]), "radius" : 4 * mm, "tangentPropagation" : true, "allowEdgeOverflow" : false});
        }
        {
            var Q0;
            Q0=makeQuery(id+"F3.opExtrude","CAP_EDGE",EDGE,{"disambiguationData":[OSD([sQuery(id+"F2.wireOp",EDGE,"E19")])],"isStart":false});
            var Q1;
            Q1=makeQuery(id+"F1.opRevolve","SWEPT_EDGE",EDGE,{"disambiguationData":[OSD([sQuery(id+"F0.wireOp",EDGE,"E11"),sQuery(id+"F0.wireOp",EDGE,"E12")])]});
            fillet(context, id + "F8", {"entities" : qUnion([Q0, Q1]), "radius" : 2 * mm, "tangentPropagation" : true, "allowEdgeOverflow" : false});
        }
        {
            var Q0;
            Q0=makeQuery(id+"F1.opRevolve","SWEPT_EDGE",EDGE,{"disambiguationData":[OSD([sQuery(id+"F0.wireOp",EDGE,"E3"),sQuery(id+"F0.wireOp",EDGE,"E4")])]});
            var Q1;
            Q1=makeQuery(id+"F1.opRevolve","SWEPT_EDGE",EDGE,{"disambiguationData":[OSD([sQuery(id+"F0.wireOp",EDGE,"E4"),sQuery(id+"F0.wireOp",EDGE,"E5")])]});
            var Q2;
            Q2=makeQuery(id+"F1.opRevolve","SWEPT_EDGE",EDGE,{"disambiguationData":[OSD([sQuery(id+"F0.wireOp",EDGE,"E7"),sQuery(id+"F0.wireOp",EDGE,"E8")])]});
            var Q3;
            Q3=makeQuery(id+"F1.opRevolve","SWEPT_EDGE",EDGE,{"disambiguationData":[OSD([sQuery(id+"F0.wireOp",EDGE,"E8"),sQuery(id+"F0.wireOp",EDGE,"E9")])]});
            chamfer(context, id + "F9", {"entities" : qUnion([Q0, Q1, Q2, Q3]), "width" : 1.5 * mm, "tangentPropagation" : true});
        }
        {
            var Q0;
            {var subQ0=sQuery(id+"F0.wireOp",EDGE,"E14");Q0=makeQuery(id+"F0.imprint","IMPRINT",FACE,{"disambiguationData":[TD([[makeQuery(id+"F0.imprint","IMPRINT",EDGE,{"derivedFrom":subQ0}),1.0]])]});}
            var Q1;
            {var subQ5=sQuery(id+"F0.wireOp",EDGE,"E18");Q1=makeQuery(id+"F0.imprint","IMPRINT",FACE,{"disambiguationData":[TD([[makeQuery(id+"F0.imprint","IMPRINT",EDGE,{"derivedFrom":subQ5}),1.0]])]});}
            var Q2;
            Q2=sQuery(id+"F0.wireOp",EDGE,"E13");
            revolve(context, id + "F10", {"entities" : qUnion([Q0, Q1]), "axis" : qUnion([Q2]), "revolveType" : RevolveType.FULL});
        }
        {
            var Q0;
            Q0=makeQuery(id+"F10.opRevolve","SWEPT_BODY",BODY,{"disambiguationData":[OSD([sQuery(id+"F0.wireOp",EDGE,"E13"),sQuery(id+"F0.wireOp",EDGE,"E14"),sQuery(id+"F0.wireOp",EDGE,"E15"),sQuery(id+"F0.wireOp",EDGE,"E16")])]});
            var Q1;
            Q1=makeQuery(id+"F5.opExtrude","SWEPT_BODY",BODY,{"disambiguationData":[OSD([sQuery(id+"F4.wireOp",EDGE,"E38"),sQuery(id+"F4.wireOp",EDGE,"E39"),sQuery(id+"F4.wireOp",EDGE,"E40"),sQuery(id+"F4.wireOp",EDGE,"E41"),sQuery(id+"F4.wireOp",EDGE,"E42"),sQuery(id+"F4.wireOp",EDGE,"E43")])]});
            booleanBodies(context, id + "F11", {"operationType" : BooleanOperationType.SUBTRACTION, "tools" : qUnion([Q0]), "targets" : qUnion([Q1])});
        }
    });
